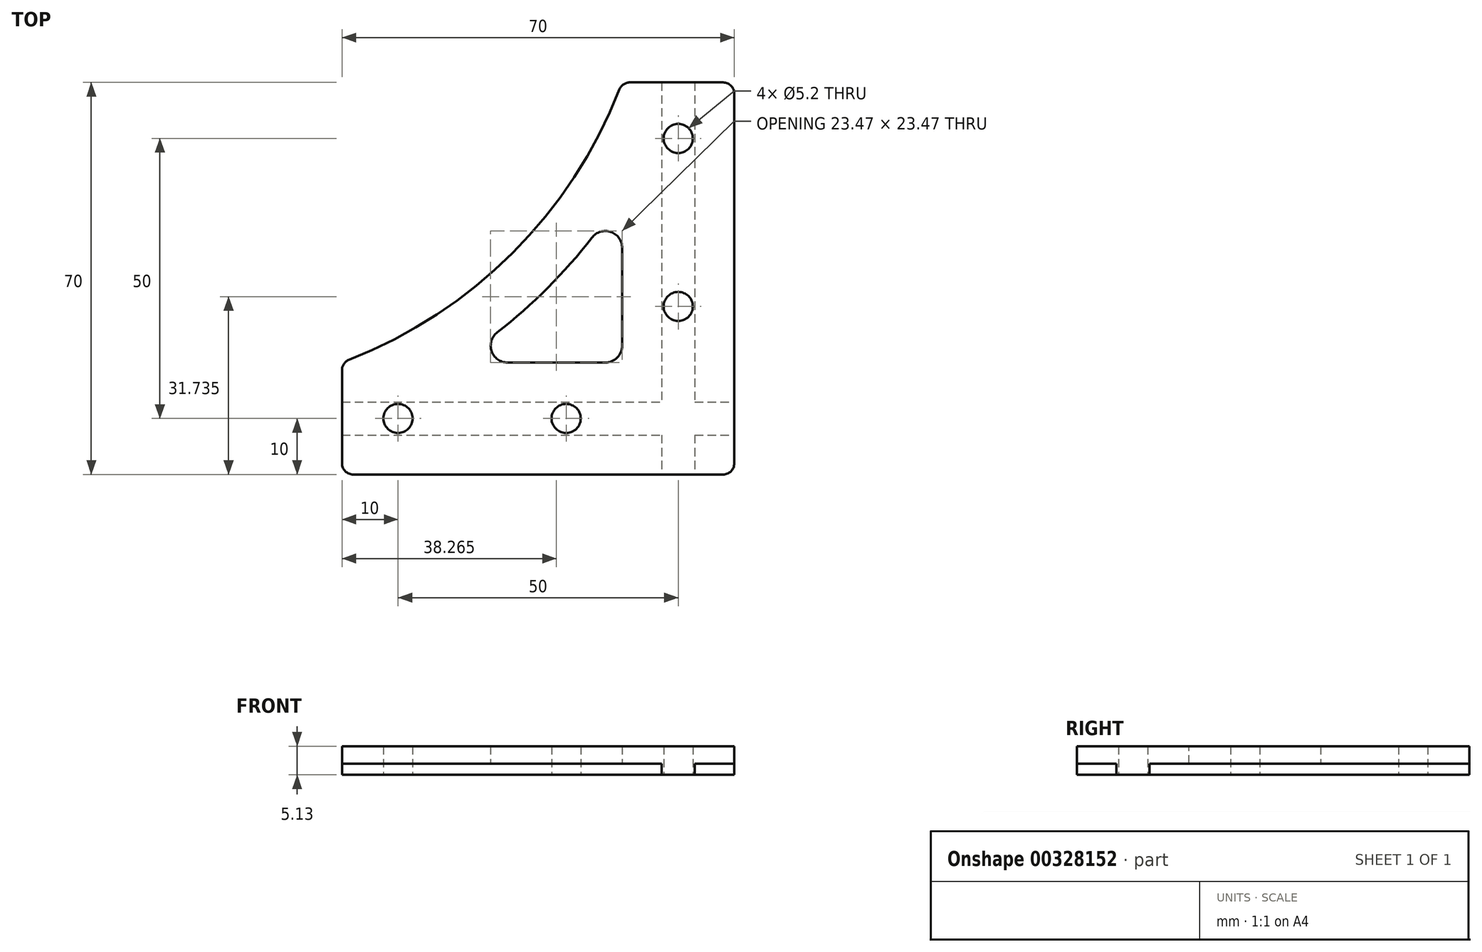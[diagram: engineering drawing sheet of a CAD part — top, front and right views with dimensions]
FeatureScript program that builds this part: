
annotation { "Feature Type Name" : "Feature", "Feature Type Description" : "" }
export const myFeature = defineFeature(function(context is Context, id is Id, definition is map)
    precondition{}
    {
        {
            var Q0;
            Q0=qCreatedBy(makeId("Top.planeOp"),FACE);
            var sketch = newSketch(context, id + "F0", { "sketchPlane" : qUnion([Q0])});
            skLineSegment(sketch, "E0.bottom", {"start": v(-35, 35) * mm, "end": v(35, 35) * mm});
            skLineSegment(sketch, "E0.top", {"start": v(-35, -35) * mm, "end": v(35, -35) * mm});
            skLineSegment(sketch, "E0.left", {"start": v(-35, 35) * mm, "end": v(-35, -35) * mm});
            skLineSegment(sketch, "E0.right", {"start": v(35, 35) * mm, "end": v(35, -35) * mm});
            skPoint(sketch, "E0.middle", {"position": v(0, 0) * mm});
            skLineSegment(sketch, "E1", {"start": v(15, 35) * mm, "end": v(-35, -15) * mm});
            skArc(sketch, "E2", {"start": v(-35, -15) * mm, "mid": v(-4.55, 4.55) * mm, "end": v(15, 35) * mm});
            skSolve(sketch);
        }
        {
            var Q0;
            {var subQ2=sQuery(id+"F0.wireOp",EDGE,"E0.top");Q0=makeQuery(id+"F0.imprint","IMPRINT",FACE,{"disambiguationData":[TD([[makeQuery(id+"F0.imprint","IMPRINT",EDGE,{"derivedFrom":subQ2}),1.0]])]});}
            extrude(context, id + "F1", {"entities" : qUnion([Q0]), "depth" : 3.12 * mm});
        }
        {
            var Q0;
            Q0=makeQuery(id+"F1.opExtrude","CAP_FACE",FACE,{"disambiguationData":[OSD([sQuery(id+"F0.wireOp",EDGE,"E0.bottom"),sQuery(id+"F0.wireOp",EDGE,"E0.top"),sQuery(id+"F0.wireOp",EDGE,"E0.left"),sQuery(id+"F0.wireOp",EDGE,"E0.right"),sQuery(id+"F0.wireOp",EDGE,"E1")])],"isStart":true});
            var sketch = newSketch(context, id + "F2", { "sketchPlane" : qUnion([Q0])});
            skLineSegment(sketch, "E3", {"start": v(25, -35) * mm, "end": v(25, 35) * mm, "construction": true});
            skLineSegment(sketch, "E4", {"start": v(-35, 25) * mm, "end": v(35, 25) * mm, "construction": true});
            skLineSegment(sketch, "E5.bottom", {"start": v(22.05, -35) * mm, "end": v(27.95, -35) * mm});
            skLineSegment(sketch, "E5.top", {"start": v(22.05, 35) * mm, "end": v(27.95, 35) * mm});
            skLineSegment(sketch, "E5.left", {"start": v(22.05, -35) * mm, "end": v(22.05, 35) * mm});
            skLineSegment(sketch, "E5.right", {"start": v(27.95, -35) * mm, "end": v(27.95, 35) * mm});
            skPoint(sketch, "E5.middle", {"position": v(25, 0) * mm});
            skLineSegment(sketch, "E6.bottom", {"start": v(-35, 22.05) * mm, "end": v(35, 22.05) * mm});
            skLineSegment(sketch, "E6.top", {"start": v(-35, 27.95) * mm, "end": v(35, 27.95) * mm});
            skLineSegment(sketch, "E6.left", {"start": v(-35, 22.05) * mm, "end": v(-35, 27.95) * mm});
            skLineSegment(sketch, "E6.right", {"start": v(35, 22.05) * mm, "end": v(35, 27.95) * mm});
            skPoint(sketch, "E6.middle", {"position": v(0, 25) * mm});
            skLineSegment(sketch, "E7.bottom", {"start": v(22.05, 22.05) * mm, "end": v(15.05, 22.05) * mm});
            skLineSegment(sketch, "E7.top", {"start": v(22.05, 27.95) * mm, "end": v(15.05, 27.95) * mm});
            skLineSegment(sketch, "E7.left", {"start": v(22.05, 22.05) * mm, "end": v(22.05, 27.95) * mm});
            skLineSegment(sketch, "E7.right", {"start": v(15.05, 22.05) * mm, "end": v(15.05, 27.95) * mm});
            skLineSegment(sketch, "E8.bottom", {"start": v(27.95, 22.05) * mm, "end": v(22.05, 22.05) * mm});
            skLineSegment(sketch, "E8.top", {"start": v(27.95, 15.05) * mm, "end": v(22.05, 15.05) * mm});
            skLineSegment(sketch, "E8.left", {"start": v(27.95, 22.05) * mm, "end": v(27.95, 15.05) * mm});
            skLineSegment(sketch, "E8.right", {"start": v(22.05, 22.05) * mm, "end": v(22.05, 15.05) * mm});
            skSolve(sketch);
        }
        {
            var Q0;
            {var subQ0=sQuery(id+"F2.wireOp",EDGE,"E5.bottom");Q0=makeQuery(id+"F2.imprint","IMPRINT",FACE,{"disambiguationData":[TD([[makeQuery(id+"F2.imprint","IMPRINT",EDGE,{"derivedFrom":subQ0}),1.0]])]});}
            var Q1;
            {var subQ0=sQuery(id+"F2.wireOp",EDGE,"E6.left");Q1=makeQuery(id+"F2.imprint","IMPRINT",FACE,{"disambiguationData":[TD([[makeQuery(id+"F2.imprint","IMPRINT",EDGE,{"derivedFrom":subQ0}),-1.0]])]});}
            var Q2;
            {var subQ0=sQuery(id+"F2.wireOp",EDGE,"E8.top");Q2=makeQuery(id+"F2.imprint","IMPRINT",FACE,{"disambiguationData":[TD([[makeQuery(id+"F2.imprint","IMPRINT",EDGE,{"derivedFrom":subQ0}),1.0]])]});}
            var Q3;
            {var subQ0=sQuery(id+"F2.wireOp",EDGE,"d9nGMlHh-qkIi-XzYH-rveG-kUuO3HYsBL67");var subQ1=sQuery(id+"F2.wireOp",EDGE,"E5.left");var subQ2=makeQuery(id+"F2.imprint","INTERSECT",VERTEX,{"derivedFrom":[subQ1,subQ0]});Q3=makeQuery(id+"F2.imprint","IMPRINT",FACE,{"disambiguationData":[TD([[makeQuery(id+"F2.imprint","IMPRINT",EDGE,{"disambiguationData":[TD([[subQ2,-1.0]])],"derivedFrom":subQ1}),-1.0]])]});}
            var Q4;
            {var subQ0=sQuery(id+"F2.wireOp",EDGE,"E7.right");Q4=makeQuery(id+"F2.imprint","IMPRINT",FACE,{"disambiguationData":[TD([[makeQuery(id+"F2.imprint","IMPRINT",EDGE,{"derivedFrom":subQ0}),1.0]])]});}
            var Q5;
            {var subQ0=sQuery(id+"F2.wireOp",EDGE,"Tg9qOg1b-ZZ8D-OlWz-hFwT-lKIjL2JHWv4c");var subQ1=sQuery(id+"F2.wireOp",EDGE,"E6.bottom");var subQ2=makeQuery(id+"F2.imprint","INTERSECT",VERTEX,{"derivedFrom":[subQ1,subQ0]});Q5=makeQuery(id+"F2.imprint","IMPRINT",FACE,{"disambiguationData":[TD([[makeQuery(id+"F2.imprint","IMPRINT",EDGE,{"disambiguationData":[TD([[subQ2,-1.0]])],"derivedFrom":subQ1}),1.0]])]});}
            extrude(context, id + "F3", {"entities" : qUnion([Q0, Q1, Q2, Q3, Q4, Q5]), "operationType" : NewBodyOperationType.ADD, "depth" : 2 * mm});
        }
        {
            var Q0;
            Q0=makeQuery(id+"F3.opExtrude","CAP_FACE",FACE,{"disambiguationData":[OSD([sQuery(id+"F2.wireOp",EDGE,"E5.bottom"),sQuery(id+"F2.wireOp",EDGE,"E5.left"),sQuery(id+"F2.wireOp",EDGE,"E5.right"),sQuery(id+"F2.wireOp",EDGE,"E8.top")])],"isStart":false});
            var sketch = newSketch(context, id + "F4", { "sketchPlane" : qUnion([Q0])});
            skCircle(sketch, "E9", {"center": v(25, -25) * mm, "radius": 2.6 * mm});
            skCircle(sketch, "E10", {"center": v(25, 5) * mm, "radius": 2.6 * mm});
            skCircle(sketch, "E11", {"center": v(5, 25) * mm, "radius": 2.6 * mm});
            skCircle(sketch, "E12", {"center": v(-25, 25) * mm, "radius": 2.6 * mm});
            skSolve(sketch);
        }
        {
            var Q0;
            Q0=makeQuery(id+"F4.imprint","IMPRINT",FACE,{"disambiguationData":[TD([[makeQuery(id+"F4.imprint","IMPRINT",EDGE,{"derivedFrom":sQuery(id+"F4.wireOp",EDGE,"E9")}),1.0]])]});
            var Q1;
            Q1=makeQuery(id+"F4.imprint","IMPRINT",FACE,{"disambiguationData":[TD([[makeQuery(id+"F4.imprint","IMPRINT",EDGE,{"derivedFrom":sQuery(id+"F4.wireOp",EDGE,"E10")}),1.0]])]});
            var Q2;
            Q2=makeQuery(id+"F4.imprint","IMPRINT",FACE,{"disambiguationData":[TD([[makeQuery(id+"F4.imprint","IMPRINT",EDGE,{"derivedFrom":sQuery(id+"F4.wireOp",EDGE,"E11")}),1.0]])]});
            var Q3;
            Q3=makeQuery(id+"F4.imprint","IMPRINT",FACE,{"disambiguationData":[TD([[makeQuery(id+"F4.imprint","IMPRINT",EDGE,{"derivedFrom":sQuery(id+"F4.wireOp",EDGE,"E12")}),1.0]])]});
            extrude(context, id + "F5", {"entities" : qUnion([Q0, Q1, Q2, Q3]), "operationType" : NewBodyOperationType.REMOVE, "oppositeDirection" : true, "depth" : 25 * mm});
        }
        {
            var Q0;
            Q0=makeQuery(id+"F1.opExtrude","SWEPT_EDGE",EDGE,{"disambiguationData":[OSD([sQuery(id+"F0.wireOp",EDGE,"E0.bottom"),sQuery(id+"F0.wireOp",EDGE,"E0.right")])]});
            var Q1;
            Q1=makeQuery(id+"F1.opExtrude","SWEPT_EDGE",EDGE,{"disambiguationData":[OSD([sQuery(id+"F0.wireOp",EDGE,"E0.bottom"),sQuery(id+"F0.wireOp",EDGE,"E1")])]});
            var Q2;
            Q2=makeQuery(id+"F1.opExtrude","SWEPT_EDGE",EDGE,{"disambiguationData":[OSD([sQuery(id+"F0.wireOp",EDGE,"E0.left"),sQuery(id+"F0.wireOp",EDGE,"E1")])]});
            var Q3;
            Q3=makeQuery(id+"F1.opExtrude","SWEPT_EDGE",EDGE,{"disambiguationData":[OSD([sQuery(id+"F0.wireOp",EDGE,"E0.top"),sQuery(id+"F0.wireOp",EDGE,"E0.left")])]});
            var Q4;
            Q4=makeQuery(id+"F1.opExtrude","SWEPT_EDGE",EDGE,{"disambiguationData":[OSD([sQuery(id+"F0.wireOp",EDGE,"E0.top"),sQuery(id+"F0.wireOp",EDGE,"E0.right")])]});
            fillet(context, id + "F6", {"entities" : qUnion([Q0, Q1, Q2, Q3, Q4]), "radius" : 2 * mm, "tangentPropagation" : true, "allowEdgeOverflow" : false});
        }
        {
            var Q0;
            Q0=qCreatedBy(makeId("Top.planeOp"),FACE);
            var sketch = newSketch(context, id + "F7", { "sketchPlane" : qUnion([Q0])});
            skLineSegment(sketch, "E13.bottom", {"start": v(15, 15) * mm, "end": v(-15, 15) * mm});
            skLineSegment(sketch, "E13.top", {"start": v(15, -15) * mm, "end": v(-15, -15) * mm});
            skLineSegment(sketch, "E13.left", {"start": v(15, 15) * mm, "end": v(15, -15) * mm});
            skLineSegment(sketch, "E13.right", {"start": v(-15, 15) * mm, "end": v(-15, -15) * mm});
            skLineSegment(sketch, "E14", {"start": v(15, 15) * mm, "end": v(-15, -15) * mm});
            skArc(sketch, "E15", {"start": v(-15, -15) * mm, "mid": v(1.7, -1.7) * mm, "end": v(15, 15) * mm});
            skSolve(sketch);
        }
        {
            var Q0;
            Q0=makeQuery(id+"F7.imprint","IMPRINT",FACE,{"disambiguationData":[TD([[makeQuery(id+"F7.imprint","IMPRINT",EDGE,{"derivedFrom":sQuery(id+"F7.wireOp",EDGE,"E13.top")}),-1.0]])]});
            extrude(context, id + "F8", {"entities" : qUnion([Q0]), "operationType" : NewBodyOperationType.REMOVE, "depth" : 25 * mm});
        }
        {
            var Q0;
            Q0=makeQuery(id+"F8.boolean.opBoolean","COPY",EDGE,{"derivedFrom":makeQuery(id+"F8.opExtrude","SWEPT_EDGE",EDGE,{"disambiguationData":[OSD([sQuery(id+"F7.wireOp",EDGE,"E13.bottom"),sQuery(id+"F7.wireOp",EDGE,"E13.left"),sQuery(id+"F7.wireOp",EDGE,"E14")])]})});
            var Q1;
            Q1=makeQuery(id+"F8.boolean.opBoolean","COPY",EDGE,{"derivedFrom":makeQuery(id+"F8.opExtrude","SWEPT_EDGE",EDGE,{"disambiguationData":[OSD([sQuery(id+"F7.wireOp",EDGE,"E13.top"),sQuery(id+"F7.wireOp",EDGE,"E13.left")])]})});
            var Q2;
            Q2=makeQuery(id+"F8.boolean.opBoolean","COPY",EDGE,{"derivedFrom":makeQuery(id+"F8.opExtrude","SWEPT_EDGE",EDGE,{"disambiguationData":[OSD([sQuery(id+"F7.wireOp",EDGE,"E13.top"),sQuery(id+"F7.wireOp",EDGE,"E13.right"),sQuery(id+"F7.wireOp",EDGE,"E14")])]})});
            fillet(context, id + "F9", {"entities" : qUnion([Q0, Q1, Q2]), "radius" : 3 * mm, "tangentPropagation" : true, "allowEdgeOverflow" : false});
        }
    });
